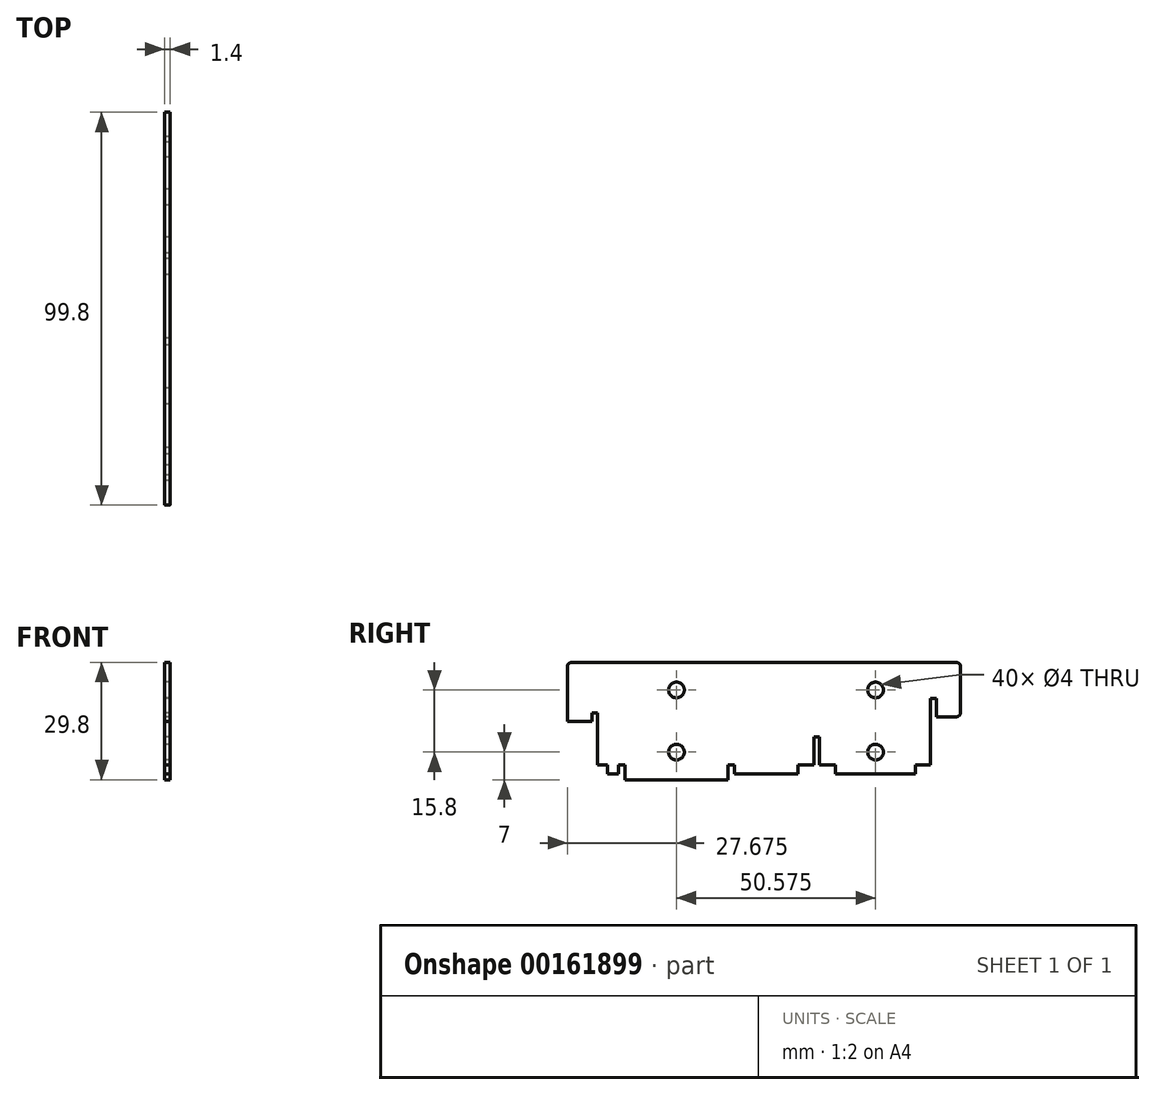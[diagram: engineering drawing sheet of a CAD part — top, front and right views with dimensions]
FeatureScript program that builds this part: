
annotation { "Feature Type Name" : "Feature", "Feature Type Description" : "" }
export const myFeature = defineFeature(function(context is Context, id is Id, definition is map)
    precondition{}
    {
        {
            var Q0;
            Q0=qCreatedBy(makeId("Right.planeOp"),FACE);
            var sketch = newSketch(context, id + "F0", { "sketchPlane" : qUnion([Q0])});
            skLineSegment(sketch, "E0.top", {"start": v(-9.2, -14.9) * mm, "end": v(-35.25, -14.9) * mm});
            skLineSegment(sketch, "E0.left", {"start": v(49.9, 14.9) * mm, "end": v(49.9, 1.1) * mm});
            skLineSegment(sketch, "E0.right", {"start": v(-49.9, 14.9) * mm, "end": v(-49.9, -13.4) * mm});
            skPoint(sketch, "E0.middle", {"position": v(0, 0) * mm});
            skLineSegment(sketch, "E1.top", {"start": v(49.9, 1.1) * mm, "end": v(43.75, 1.1) * mm});
            skLineSegment(sketch, "E1.right", {"start": v(43.75, 5.8) * mm, "end": v(43.75, 1.1) * mm});
            skLineSegment(sketch, "E2.top", {"start": v(-39.75, -13.4) * mm, "end": v(-36.95, -13.4) * mm});
            skLineSegment(sketch, "E2.left", {"start": v(-49.9, 14.9) * mm, "end": v(-49.9, 2.1) * mm});
            skLineSegment(sketch, "E3.top", {"start": v(43.75, 5.8) * mm, "end": v(42.35, 5.8) * mm});
            skLineSegment(sketch, "E4.top", {"start": v(42.35, -11.1) * mm, "end": v(38.5, -11.1) * mm});
            skLineSegment(sketch, "E4.left", {"start": v(42.35, 5.8) * mm, "end": v(42.35, -11.1) * mm});
            skLineSegment(sketch, "E5.top", {"start": v(38.5, -13.4) * mm, "end": v(18.2, -13.4) * mm});
            skLineSegment(sketch, "E5.left", {"start": v(38.5, -11.1) * mm, "end": v(38.5, -13.4) * mm});
            skLineSegment(sketch, "E6.top", {"start": v(18.2, -11.1) * mm, "end": v(14.15, -11.1) * mm});
            skLineSegment(sketch, "E6.left", {"start": v(18.2, -13.4) * mm, "end": v(18.2, -11.1) * mm});
            skLineSegment(sketch, "E6.right", {"start": v(8.7, -13.4) * mm, "end": v(8.7, -11.1) * mm});
            skPoint(sketch, "E7.endSnap0", {"position": v(13.45, -11.1) * mm});
            skLineSegment(sketch, "E8.right", {"start": v(14.15, -4) * mm, "end": v(14.15, -11.1) * mm});
            skLineSegment(sketch, "E9.right", {"start": v(12.75, -4) * mm, "end": v(12.75, -11.1) * mm});
            skPoint(sketch, "E9.bottom.start.orphan", {"position": v(13.45, -4.4) * mm});
            skLineSegment(sketch, "E10", {"start": v(14.15, -4) * mm, "end": v(12.75, -4) * mm});
            skLineSegment(sketch, "E11.trimOffspring", {"start": v(12.75, -11.1) * mm, "end": v(8.7, -11.1) * mm});
            skPoint(sketch, "E7.start.orphan", {"position": v(13.45, -13.4) * mm});
            skLineSegment(sketch, "E12.trimOffspring", {"start": v(18.2, -13.4) * mm, "end": v(38.5, -13.4) * mm});
            skLineSegment(sketch, "E13.bottom", {"start": v(8.7, -13.4) * mm, "end": v(-7.5, -13.4) * mm});
            skLineSegment(sketch, "E13.right", {"start": v(-7.5, -13.4) * mm, "end": v(-7.5, -11.2) * mm});
            skLineSegment(sketch, "E14.right", {"start": v(-9.2, -13.4) * mm, "end": v(-9.2, -11.2) * mm});
            skLineSegment(sketch, "E15.bottom", {"start": v(-9.2, -11.2) * mm, "end": v(-7.5, -11.2) * mm});
            skLineSegment(sketch, "E15.left", {"start": v(-9.2, -11.2) * mm, "end": v(-9.2, -14.9) * mm});
            skLineSegment(sketch, "E15.right", {"start": v(-7.5, -11.2) * mm, "end": v(-7.5, -13.4) * mm});
            skLineSegment(sketch, "E16.trimOffspring", {"start": v(-7.5, -13.4) * mm, "end": v(8.7, -13.4) * mm});
            skPoint(sketch, "E17.orphan", {"position": v(-7.5, -14.9) * mm});
            skPoint(sketch, "E18.orphan", {"position": v(49.9, -14.9) * mm});
            skLineSegment(sketch, "E19.left", {"start": v(-9.2, -14.9) * mm, "end": v(-9.2, -11.2) * mm});
            skLineSegment(sketch, "E19.right", {"start": v(-35.25, -14.9) * mm, "end": v(-35.25, -13.4) * mm});
            skLineSegment(sketch, "E20.top", {"start": v(-35.25, -11.2) * mm, "end": v(-36.95, -11.2) * mm});
            skLineSegment(sketch, "E20.left", {"start": v(-35.25, -13.4) * mm, "end": v(-35.25, -11.2) * mm});
            skLineSegment(sketch, "E20.right", {"start": v(-36.95, -13.4) * mm, "end": v(-36.95, -11.2) * mm});
            skPoint(sketch, "E21.orphan", {"position": v(-49.9, -14.9) * mm});
            skLineSegment(sketch, "E22.bottom", {"start": v(-36.95, -13.4) * mm, "end": v(-39.75, -13.4) * mm});
            skLineSegment(sketch, "E22.right", {"start": v(-39.75, -13.4) * mm, "end": v(-39.75, -11.1) * mm});
            skLineSegment(sketch, "E23.bottom", {"start": v(-39.75, -11.1) * mm, "end": v(-42.25, -11.1) * mm});
            skLineSegment(sketch, "E23.right", {"start": v(-42.25, -11.1) * mm, "end": v(-42.25, 2.1) * mm});
            skLineSegment(sketch, "E24.right", {"start": v(-49.9, 6.44) * mm, "end": v(-49.9, 2.1) * mm});
            skLineSegment(sketch, "E25", {"start": v(-49.9, 14.9) * mm, "end": v(49.9, 14.9) * mm});
            skLineSegment(sketch, "E26", {"start": v(-43.65, 2.1) * mm, "end": v(-42.25, 2.1) * mm});
            skLineSegment(sketch, "E27.top", {"start": v(-43.65, -0.1) * mm, "end": v(-49.9, -0.1) * mm});
            skLineSegment(sketch, "E27.left", {"start": v(-43.65, 2.1) * mm, "end": v(-43.65, -0.1) * mm});
            skLineSegment(sketch, "E27.right", {"start": v(-49.9, 2.1) * mm, "end": v(-49.9, -0.1) * mm});
            skCircle(sketch, "E28", {"center": v(-22.22, 7.9) * mm, "radius": 2 * mm});
            skCircle(sketch, "E29", {"center": v(-22.22, -7.9) * mm, "radius": 2 * mm});
            skCircle(sketch, "E30", {"center": v(28.35, 7.9) * mm, "radius": 2 * mm});
            skCircle(sketch, "E31", {"center": v(28.35, -7.9) * mm, "radius": 2 * mm});
            skPoint(sketch, "E32.orphan", {"position": v(-49.9, -7.9) * mm});
            skPoint(sketch, "E33.start.orphan", {"position": v(-22.22, -14.9) * mm});
            skPoint(sketch, "E34.start.orphan", {"position": v(28.35, -13.4) * mm});
            skPoint(sketch, "E35.end.orphan", {"position": v(49.9, -7.9) * mm});
            skSolve(sketch);
        }
        {
            var Q0;
            Q0=makeQuery(id+"F0.imprint","IMPRINT",FACE,{"disambiguationData":[TD([[makeQuery(id+"F0.imprint","IMPRINT",EDGE,{"derivedFrom":sQuery(id+"F0.wireOp",EDGE,"E0.left")}),-1.0]])]});
            extrude(context, id + "F1", {"entities" : qUnion([Q0]), "depth" : 1.4 * mm});
        }
        {
            var Q0;
            Q0=makeQuery(id+"F1.opExtrude","SWEPT_EDGE",EDGE,{"disambiguationData":[OSD([sQuery(id+"F0.wireOp",EDGE,"E2.left"),sQuery(id+"F0.wireOp",EDGE,"E25")])]});
            var Q1;
            Q1=makeQuery(id+"F1.opExtrude","SWEPT_EDGE",EDGE,{"disambiguationData":[OSD([sQuery(id+"F0.wireOp",EDGE,"E0.left"),sQuery(id+"F0.wireOp",EDGE,"E25")])]});
            var Q2;
            Q2=makeQuery(id+"F1.opExtrude","SWEPT_EDGE",EDGE,{"disambiguationData":[OSD([sQuery(id+"F0.wireOp",EDGE,"E0.left"),sQuery(id+"F0.wireOp",EDGE,"E1.top")])]});
            var Q3;
            Q3=makeQuery(id+"F1.opExtrude","SWEPT_EDGE",EDGE,{"disambiguationData":[OSD([sQuery(id+"F0.wireOp",EDGE,"E24.top"),sQuery(id+"F0.wireOp",EDGE,"E24.right")])]});
            fillet(context, id + "F2", {"entities" : qUnion([Q0, Q1, Q2, Q3]), "radius" : 1 * mm, "tangentPropagation" : true, "allowEdgeOverflow" : false});
        }
    });
